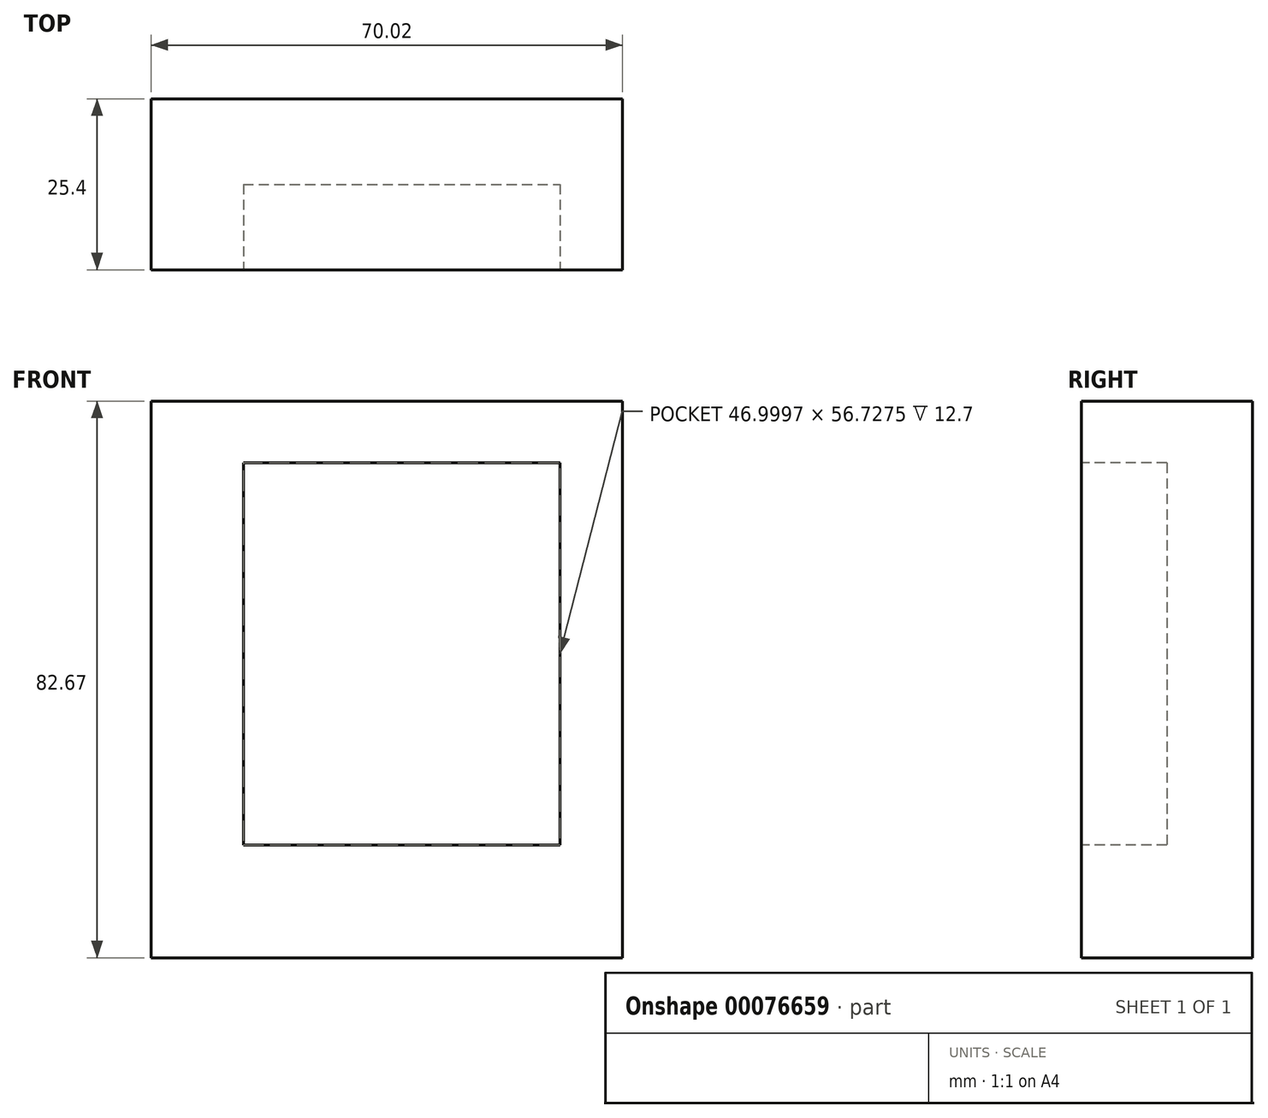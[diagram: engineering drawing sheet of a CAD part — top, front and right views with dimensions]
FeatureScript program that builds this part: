
annotation { "Feature Type Name" : "Feature", "Feature Type Description" : "" }
export const myFeature = defineFeature(function(context is Context, id is Id, definition is map)
    precondition{}
    {
        {
            var Q0;
            Q0=qCreatedBy(makeId("Front.planeOp"),FACE);
            var sketch = newSketch(context, id + "F0", { "sketchPlane" : qUnion([Q0])});
            skLineSegment(sketch, "E0.bottom", {"start": v(-42.71, 56.64) * mm, "end": v(27.31, 56.64) * mm});
            skLineSegment(sketch, "E0.top", {"start": v(-42.71, -26.03) * mm, "end": v(27.31, -26.03) * mm});
            skLineSegment(sketch, "E0.left", {"start": v(-42.71, 56.64) * mm, "end": v(-42.71, -26.03) * mm});
            skLineSegment(sketch, "E0.right", {"start": v(27.31, 56.64) * mm, "end": v(27.31, -26.03) * mm});
            skSolve(sketch);
        }
        {
            var Q0;
            Q0=makeQuery(id+"F0.imprint","IMPRINT",FACE,{"disambiguationData":[TD([[makeQuery(id+"F0.imprint","IMPRINT",EDGE,{"derivedFrom":sQuery(id+"F0.wireOp",EDGE,"E0.bottom")}),-1.0]])]});
            extrude(context, id + "F3", {"entities" : qUnion([Q0]), "depth" : 25.4 * mm});
        }
        {
            var Q0;
            Q0=makeQuery(id+"F3.opExtrude","CAP_FACE",FACE,{"disambiguationData":[OSD([sQuery(id+"F0.wireOp",EDGE,"E0.bottom"),sQuery(id+"F0.wireOp",EDGE,"E0.top"),sQuery(id+"F0.wireOp",EDGE,"E0.left"),sQuery(id+"F0.wireOp",EDGE,"E0.right")])],"isStart":false});
            var sketch = newSketch(context, id + "F1", { "sketchPlane" : qUnion([Q0])});
            skLineSegment(sketch, "E1.bottom", {"start": v(-29, 47.46) * mm, "end": v(18, 47.46) * mm});
            skLineSegment(sketch, "E1.top", {"start": v(-29, -9.27) * mm, "end": v(18, -9.27) * mm});
            skLineSegment(sketch, "E1.left", {"start": v(-29, 47.46) * mm, "end": v(-29, -9.27) * mm});
            skLineSegment(sketch, "E1.right", {"start": v(18, 47.46) * mm, "end": v(18, -9.27) * mm});
            skSolve(sketch);
        }
        {
            var Q0;
            Q0 = qSketchRegion(id + "F1", true);
            extrude(context, id + "F2", {"entities" : qUnion([Q0]), "operationType" : NewBodyOperationType.REMOVE, "oppositeDirection" : true, "depth" : 12.7 * mm});
        }
    });
